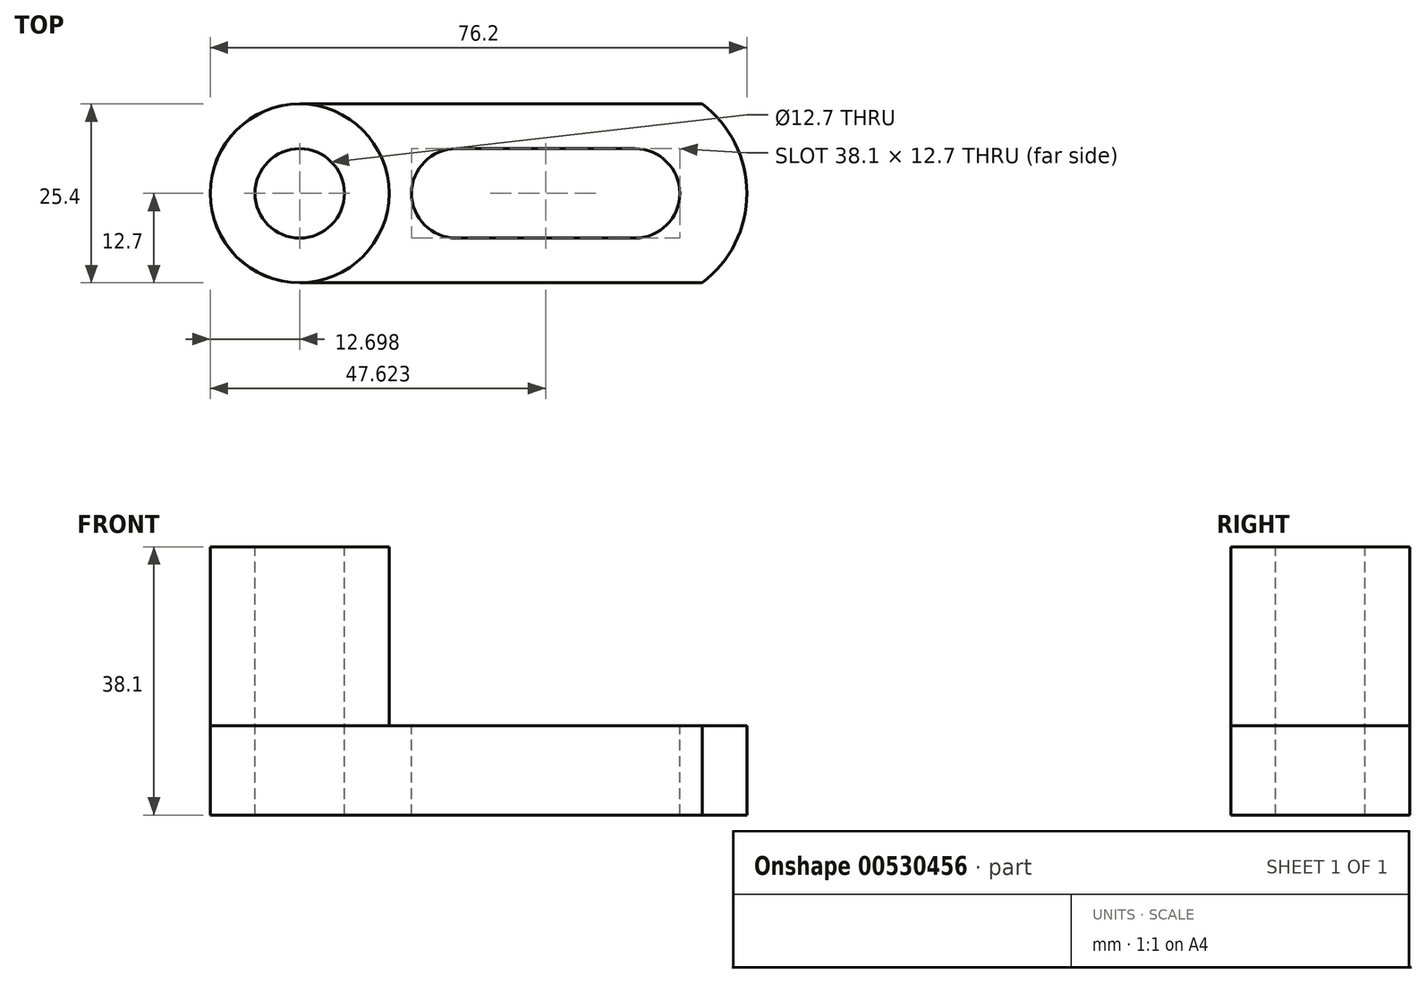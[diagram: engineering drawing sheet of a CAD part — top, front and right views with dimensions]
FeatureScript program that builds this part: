
annotation { "Feature Type Name" : "Feature", "Feature Type Description" : "" }
export const myFeature = defineFeature(function(context is Context, id is Id, definition is map)
    precondition{}
    {
        {
            var Q0;
            Q0=qCreatedBy(makeId("Front.planeOp"),FACE);
            var sketch = newSketch(context, id + "F0", { "sketchPlane" : qUnion([Q0])});
            skLineSegment(sketch, "E0", {"start": v(-67.9, 47.16) * mm, "end": v(-67.9, 12.65) * mm});
            skLineSegment(sketch, "E1", {"start": v(-67.9, 12.65) * mm, "end": v(8.3, 12.65) * mm});
            skLineSegment(sketch, "E2", {"start": v(8.3, 12.65) * mm, "end": v(8.3, 25.35) * mm});
            skLineSegment(sketch, "E3", {"start": v(8.3, 25.35) * mm, "end": v(-42.5, 25.35) * mm});
            skLineSegment(sketch, "E4", {"start": v(-42.5, 25.35) * mm, "end": v(-42.5, 50.75) * mm});
            skLineSegment(sketch, "E5", {"start": v(-42.5, 50.75) * mm, "end": v(-67.9, 50.75) * mm});
            skLineSegment(sketch, "E6", {"start": v(-67.9, 50.75) * mm, "end": v(-67.9, 47.16) * mm});
            skSolve(sketch);
        }
        {
            var Q0;
            Q0=makeQuery(id+"F0.imprint","IMPRINT",FACE,{"disambiguationData":[TD([[makeQuery(id+"F0.imprint","IMPRINT",EDGE,{"derivedFrom":sQuery(id+"F0.wireOp",EDGE,"E0")}),1.0]])]});
            extrude(context, id + "F1", {"entities" : qUnion([Q0]), "depth" : 25.4 * mm, "offsetDistance" : 25.4 * mm});
        }
        {
            var Q0;
            Q0=makeQuery(id+"F1.opExtrude","SWEPT_FACE",FACE,{"disambiguationData":[OSD([sQuery(id+"F0.wireOp",EDGE,"E3")])]});
            var sketch = newSketch(context, id + "F2", { "sketchPlane" : qUnion([Q0])});
            skArc(sketch, "E7", {"start": v(1.96, -25.4) * mm, "mid": v(8.3, -12.7) * mm, "end": v(1.96, 0) * mm});
            skSolve(sketch);
        }
        {
            var Q0;
            {var subQ0=sQuery(id+"F2.wireOp",EDGE,"E7");var subQ1=sQuery(id+"F0.wireOp",EDGE,"E3");var subQ2=makeQuery(id+"F1.opExtrude","CAP_EDGE",EDGE,{"disambiguationData":[OSD([subQ1])],"isStart":true});var subQ3=makeQuery(id+"F2.imprint","INTERSECT",VERTEX,{"derivedFrom":[subQ2,subQ0]});Q0=makeQuery(id+"F2.imprint","IMPRINT",FACE,{"disambiguationData":[TD([[makeQuery(id+"F2.imprint","IMPRINT",EDGE,{"disambiguationData":[TD([[subQ3,1.0]])],"derivedFrom":subQ0}),-1.0]])]});}
            var Q1;
            {var subQ0=sQuery(id+"F2.wireOp",EDGE,"E7");var subQ1=sQuery(id+"F0.wireOp",EDGE,"E3");var subQ2=makeQuery(id+"F1.opExtrude","CAP_EDGE",EDGE,{"disambiguationData":[OSD([subQ1])],"isStart":false});var subQ3=makeQuery(id+"F2.imprint","INTERSECT",VERTEX,{"derivedFrom":[subQ2,subQ0]});Q1=makeQuery(id+"F2.imprint","IMPRINT",FACE,{"disambiguationData":[TD([[makeQuery(id+"F2.imprint","IMPRINT",EDGE,{"disambiguationData":[TD([[subQ3,-1.0]])],"derivedFrom":subQ0}),-1.0]])]});}
            extrude(context, id + "F3", {"entities" : qUnion([Q0, Q1]), "operationType" : NewBodyOperationType.REMOVE, "endBound" : BoundingType.THROUGH_ALL, "oppositeDirection" : true, "depth" : 25.4 * mm, "offsetDistance" : 25.4 * mm});
        }
        {
            var Q0;
            Q0=makeQuery(id+"F1.opExtrude","SWEPT_FACE",FACE,{"disambiguationData":[OSD([sQuery(id+"F0.wireOp",EDGE,"E5")])]});
            var sketch = newSketch(context, id + "F4", { "sketchPlane" : qUnion([Q0])});
            skCircle(sketch, "E8", {"center": v(-55.2, -12.7) * mm, "radius": 12.7 * mm});
            skSolve(sketch);
        }
        {
            var Q0;
            {var subQ0=sQuery(id+"F4.wireOp",EDGE,"E8");var subQ1=sQuery(id+"F0.wireOp",EDGE,"E5");var subQ2=makeQuery(id+"F1.opExtrude","CAP_EDGE",EDGE,{"disambiguationData":[OSD([subQ1])],"isStart":true});var subQ3=makeQuery(id+"F4.imprint","INTERSECT",VERTEX,{"derivedFrom":[subQ2,subQ0]});Q0=makeQuery(id+"F4.imprint","IMPRINT",FACE,{"disambiguationData":[TD([[makeQuery(id+"F4.imprint","IMPRINT",EDGE,{"disambiguationData":[TD([[subQ3,-1.0]])],"derivedFrom":subQ0}),-1.0]])]});}
            var Q1;
            {var subQ0=sQuery(id+"F4.wireOp",EDGE,"E8");var subQ1=sQuery(id+"F0.wireOp",EDGE,"E5");var subQ4=makeQuery(id+"F1.opExtrude","CAP_EDGE",EDGE,{"disambiguationData":[OSD([subQ1])],"isStart":false});var subQ5=makeQuery(id+"F4.imprint","INTERSECT",VERTEX,{"derivedFrom":[subQ4,subQ0]});Q1=makeQuery(id+"F4.imprint","IMPRINT",FACE,{"disambiguationData":[TD([[makeQuery(id+"F4.imprint","IMPRINT",EDGE,{"disambiguationData":[TD([[subQ5,1.0]])],"derivedFrom":subQ0}),-1.0]])]});}
            extrude(context, id + "F5", {"entities" : qUnion([Q0, Q1]), "operationType" : NewBodyOperationType.REMOVE, "endBound" : BoundingType.THROUGH_ALL, "oppositeDirection" : true, "depth" : 25.4 * mm, "offsetDistance" : 25.4 * mm});
        }
        {
            var Q0;
            Q0=makeQuery(id+"F1.opExtrude","SWEPT_FACE",FACE,{"disambiguationData":[OSD([sQuery(id+"F0.wireOp",EDGE,"E5")])]});
            var sketch = newSketch(context, id + "F6", { "sketchPlane" : qUnion([Q0])});
            skCircle(sketch, "E9", {"center": v(-55.2, -12.7) * mm, "radius": 12.69 * mm});
            skSolve(sketch);
        }
        {
            var Q0;
            Q0=makeQuery(id+"F6.imprint","IMPRINT",FACE,{"disambiguationData":[TD([[makeQuery(id+"F6.imprint","IMPRINT",EDGE,{"derivedFrom":sQuery(id+"F6.wireOp",EDGE,"E9")}),-1.0]])]});
            extrude(context, id + "F7", {"entities" : qUnion([Q0]), "operationType" : NewBodyOperationType.REMOVE, "oppositeDirection" : true, "depth" : 25.4 * mm, "offsetDistance" : 25.4 * mm});
        }
        {
            var Q0;
            Q0=makeQuery(id+"F1.opExtrude","SWEPT_FACE",FACE,{"disambiguationData":[OSD([sQuery(id+"F0.wireOp",EDGE,"E5")])]});
            var sketch = newSketch(context, id + "F8", { "sketchPlane" : qUnion([Q0])});
            skCircle(sketch, "E10", {"center": v(-55.2, -12.7) * mm, "radius": 6.35 * mm});
            skSolve(sketch);
        }
        {
            var Q0;
            Q0=makeQuery(id+"F8.imprint","IMPRINT",FACE,{"disambiguationData":[TD([[makeQuery(id+"F8.imprint","IMPRINT",EDGE,{"derivedFrom":sQuery(id+"F8.wireOp",EDGE,"E10")}),1.0]])]});
            extrude(context, id + "F9", {"entities" : qUnion([Q0]), "operationType" : NewBodyOperationType.REMOVE, "endBound" : BoundingType.THROUGH_ALL, "oppositeDirection" : true, "depth" : 25.4 * mm, "offsetDistance" : 25.4 * mm});
        }
        {
            var Q0;
            Q0=makeQuery(id+"F7.boolean.opBoolean","MERGE",FACE,{"derivedFrom":[makeQuery(id+"F1.opExtrude","SWEPT_FACE",FACE,{"disambiguationData":[OSD([sQuery(id+"F0.wireOp",EDGE,"E3")])]}),makeQuery(id+"F7.opExtrude","CAP_FACE",FACE,{"disambiguationData":[OSD([sQuery(id+"F0.wireOp",EDGE,"E4"),sQuery(id+"F0.wireOp",EDGE,"E5"),sQuery(id+"F4.wireOp",EDGE,"E8"),sQuery(id+"F6.wireOp",EDGE,"E9")])],"isStart":false})]});
            var sketch = newSketch(context, id + "F10", { "sketchPlane" : qUnion([Q0])});
            skCircle(sketch, "E11", {"center": v(-7.57, -12.7) * mm, "radius": 6.35 * mm});
            skCircle(sketch, "E12", {"center": v(-32.97, -12.7) * mm, "radius": 6.35 * mm});
            skLineSegment(sketch, "E13", {"start": v(-32.97, -12.7) * mm, "end": v(-32.97, -6.35) * mm});
            skLineSegment(sketch, "E14", {"start": v(-32.97, -6.35) * mm, "end": v(-7.57, -6.35) * mm});
            skLineSegment(sketch, "E15", {"start": v(-7.57, -6.35) * mm, "end": v(-7.57, -19.05) * mm});
            skLineSegment(sketch, "E16", {"start": v(-7.57, -19.05) * mm, "end": v(-32.97, -19.05) * mm});
            skLineSegment(sketch, "E17", {"start": v(-32.97, -19.05) * mm, "end": v(-32.97, -12.7) * mm});
            skSolve(sketch);
        }
        {
            var Q0;
            Q0 = qSketchRegion(id + "F10", true);
            extrude(context, id + "F11", {"entities" : qUnion([Q0]), "operationType" : NewBodyOperationType.REMOVE, "endBound" : BoundingType.THROUGH_ALL, "oppositeDirection" : true, "depth" : 25.4 * mm, "offsetDistance" : 25.4 * mm});
        }
    });
